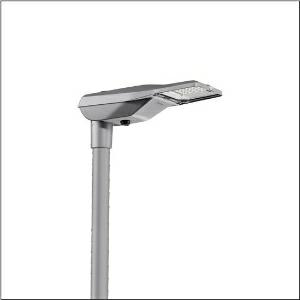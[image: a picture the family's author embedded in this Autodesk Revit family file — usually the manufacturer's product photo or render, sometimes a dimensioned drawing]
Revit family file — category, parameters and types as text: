
# Revit family: streetlight_sl_21_micro___st1_0ab_5xe1m33r08db_c8c0
name_source: partatom
category: Lighting Fixtures
units: mm (PartAtom-declared; Revit-internal decimal feet)

## family parameters
Cut with Voids When Loaded = No
Host = Face
Light Source = No
Part Type = Normal
Room Calculation Point = No
Round Connector Dimension = Use Diameter
Shared = No

## types (1)
- --- (1 x LED, 4500 lm, 39.1 W, 3000K)
    Apparent Load = 39 VA
    CIE Flux Codes = 38 73 97 100 100
    Color Rendering = 70
    Color Temperature = 3000K
    Default Elevation = 1800 mm
    Description = Streetlight SL 21 micro, mast luminaire, primary light control with lens, of PMMA, primary optical cover: cover, of toughened safety glass, transparent, light distribution: ST1.0aB, light emission: direct distribution, primary light characteristic: asymmetric, installation type: side-entry, post-top, LED, High Power LED, rated luminous flux: 4.500lm, luminous efficacy: 115lm/W, light colour: 730, colour temperature: 3000K, control gear: D4i, control: flexible luminous flux parameterisation, time-dependent luminous flux control, constant luminous flux control, overheat protection, pre-setting: logarithmic dimming characteristic, mains connection: 220..240V, AC, 50/60Hz, start of lifetime: 39W, end of service life: 41W, reduction: 18W, luminaire housing, of diecast aluminium, powder-coated, Siteco® metallic grey (DB 702S), corrosivity category C5 mid according to DIN EN ISO 12944, please order mast flange separately, inclination adjustable: 0°, 5°, 10°, 15°, sealing non-destructively replaceable, multi-level sealing system, length: 528mm, width: 235mm, height: 110mm, mast flange for spigot size: 42mm (side-entry): 5XC10008XM4, 60/48mm (side-entry/post-top): 5XC10108XM2, 76/60mm (side-entry/post-top): 5XC10108XM1, Smart Interface below, protection rating (complete): IP66, insulation class (complete): insulation class II (safety insulation), certification: CE, ENEC, ENEC+, VDE, impact resistance: IK10, permissible operating ambient temperature for outdoor applications: -40..+50°C, standard-compliant lighting for roads and squares, packaging unit: 1 piece

Light Distribution: ST1.0aB
    Height = 110 mm
    Lamp = 1 x LED
    Lamp Light Flux = 4500 lm
    Lamp Power = 39.1 W
    Lamp count = 1
    Length = 528 mm
    Luminous efficacy = 115 lm/W
    Manufacturer = Siteco
    ModVariant = No
    Model = 5XE1M33R08DB
    Number of Poles = 1
    OnlyDefault = Yes
    Power Factor = 1
    Product Name = Streetlight SL 21 micro | ST1.0aB
    Product group = mast luminaire | pylon top
    ProductGroupID = 6100
    Protection Class = Protection class II
    Protection Degree = IP 66
    RLX_Detail_Level = 1
    RLX_Emergency_Light_Flux = 0 lm
    RLX_Emergency_Type = 0
    RLX_Emergency_Type_DB = No
    RlxData = <blob elided: 98785 chars, md5=8015699c>
    Socket = socket
    Standby Power = 0 W
    System Light Flux = 4500 lm
    System Power = 39 W
    Type Comments = factory setting: luminous flux: 100 % | dim-lin: 254 | 765 mA
    Type Image = l_1277290.jpg
    URL = http://relux.com
    VarID = @adj_175495
    Voltage = 0 V
    Weight = 0.00 kg
    Width = 235 mm

## geometry (parser evidence)
native form markers: Blend x4, Sweep x11
no freeform markers — native parametric forms only
